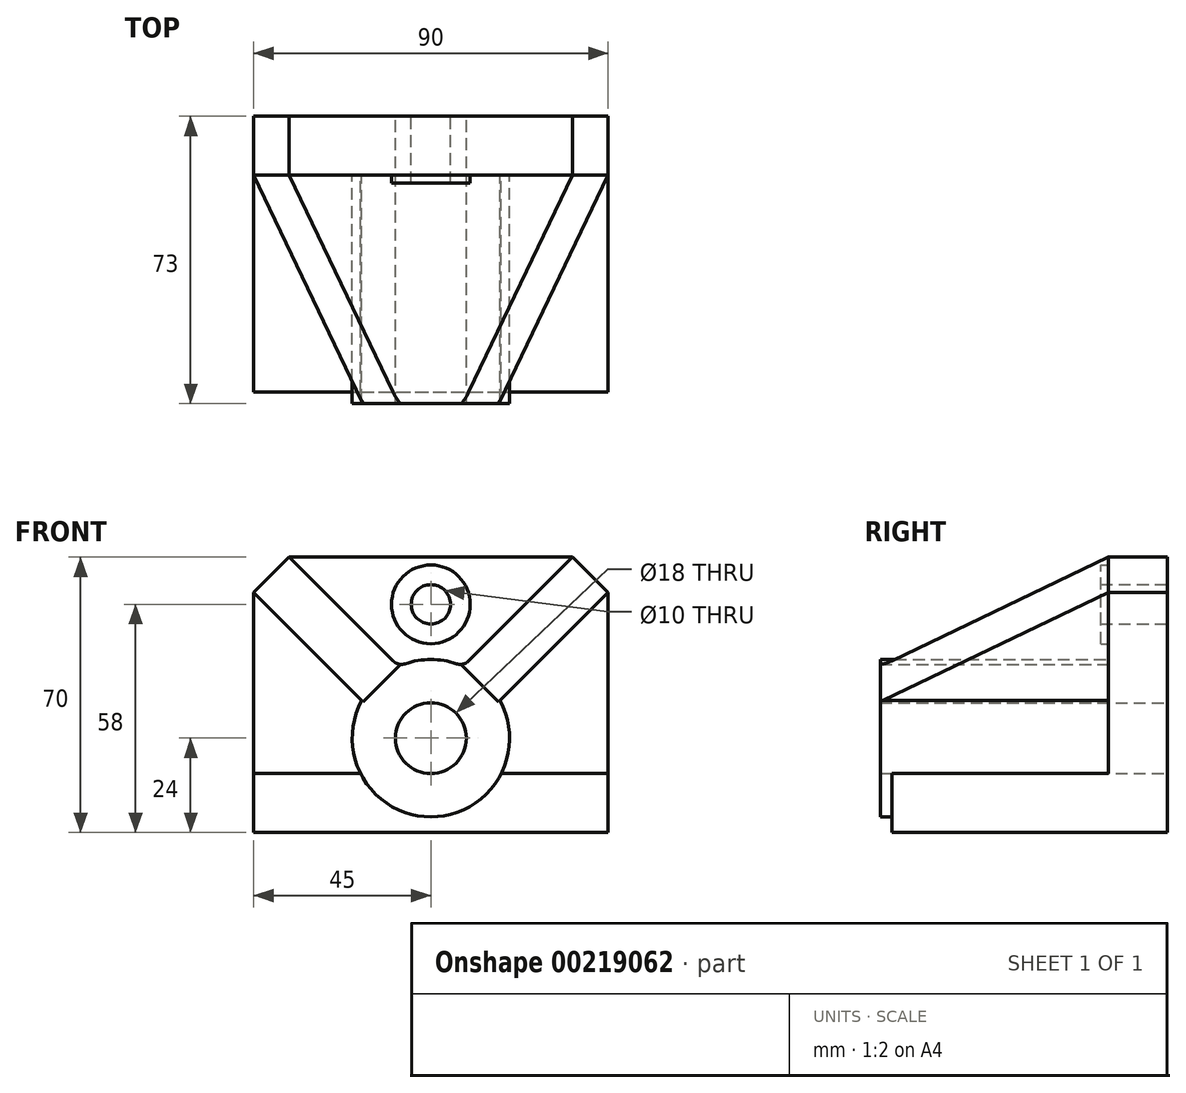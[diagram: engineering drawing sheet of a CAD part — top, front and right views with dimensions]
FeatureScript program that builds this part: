
annotation { "Feature Type Name" : "Feature", "Feature Type Description" : "" }
export const myFeature = defineFeature(function(context is Context, id is Id, definition is map)
    precondition{}
    {
        {
            var Q0;
            Q0=qCreatedBy(makeId("Front.planeOp"),FACE);
            var sketch = newSketch(context, id + "F0", { "sketchPlane" : qUnion([Q0])});
            skLineSegment(sketch, "E0", {"start": v(0, 0) * mm, "end": v(90, 0) * mm});
            skLineSegment(sketch, "E1", {"start": v(90, 0) * mm, "end": v(90, 70) * mm});
            skLineSegment(sketch, "E2", {"start": v(0, 70) * mm, "end": v(0, 0) * mm});
            skCircle(sketch, "E3", {"center": v(45, 24) * mm, "radius": 20 * mm});
            skCircle(sketch, "E4", {"center": v(45, 24) * mm, "radius": 9 * mm});
            skCircle(sketch, "E5", {"center": v(45, 58) * mm, "radius": 5 * mm});
            skCircle(sketch, "E6", {"center": v(45, 58) * mm, "radius": 10 * mm});
            skLineSegment(sketch, "E7", {"start": v(0, 15) * mm, "end": v(27.14, 15) * mm});
            skLineSegment(sketch, "E8", {"start": v(0, 70) * mm, "end": v(90, 70) * mm});
            skLineSegment(sketch, "E9.trimOffspring", {"start": v(62.86, 15) * mm, "end": v(90, 15) * mm});
            skSolve(sketch);
        }
        {
            var Q0;
            Q0=makeQuery(id+"F0.imprint","IMPRINT",FACE,{"disambiguationData":[TD([[makeQuery(id+"F0.imprint","IMPRINT",EDGE,{"derivedFrom":sQuery(id+"F0.wireOp",EDGE,"E6")}),-1.0]])]});
            extrude(context, id + "F1", {"entities" : qUnion([Q0]), "depth" : 15 * mm});
        }
        {
            var Q0;
            {var subQ4=sQuery(id+"F0.wireOp",EDGE,"E0");Q0=makeQuery(id+"F0.imprint","IMPRINT",FACE,{"disambiguationData":[TD([[makeQuery(id+"F0.imprint","IMPRINT",EDGE,{"derivedFrom":subQ4}),1.0]])]});}
            extrude(context, id + "F2", {"entities" : qUnion([Q0]), "operationType" : NewBodyOperationType.ADD, "depth" : 70 * mm});
        }
        {
            var Q0;
            Q0=makeQuery(id+"F0.imprint","IMPRINT",FACE,{"disambiguationData":[TD([[makeQuery(id+"F0.imprint","IMPRINT",EDGE,{"derivedFrom":sQuery(id+"F0.wireOp",EDGE,"E4")}),-1.0]])]});
            extrude(context, id + "F3", {"entities" : qUnion([Q0]), "operationType" : NewBodyOperationType.ADD, "depth" : 73 * mm});
        }
        {
            var Q0;
            Q0=makeQuery(id+"F0.imprint","IMPRINT",FACE,{"disambiguationData":[TD([[makeQuery(id+"F0.imprint","IMPRINT",EDGE,{"derivedFrom":sQuery(id+"F0.wireOp",EDGE,"E5")}),-1.0]])]});
            extrude(context, id + "F4", {"entities" : qUnion([Q0]), "operationType" : NewBodyOperationType.ADD, "depth" : 17 * mm});
        }
        {
            var Q0;
            Q0=makeQuery(id+"F1.opExtrude","SWEPT_EDGE",EDGE,{"disambiguationData":[OSD([sQuery(id+"F0.wireOp",EDGE,"E1"),sQuery(id+"F0.wireOp",EDGE,"E8")])]});
            var Q1;
            Q1=makeQuery(id+"F1.opExtrude","SWEPT_EDGE",EDGE,{"disambiguationData":[OSD([sQuery(id+"F0.wireOp",EDGE,"E2"),sQuery(id+"F0.wireOp",EDGE,"E8")])]});
            chamfer(context, id + "F5", {"entities" : qUnion([Q0, Q1]), "chamferType" : ChamferType.TWO_OFFSETS, "width1" : 9 * mm, "oppositeDirection" : false, "width2" : 9 * mm, "tangentPropagation" : true});
        }
        {
            var Q0;
            Q0=makeQuery(id+"F1.opExtrude","CAP_FACE",FACE,{"disambiguationData":[OSD([sQuery(id+"F0.wireOp",EDGE,"E1"),sQuery(id+"F0.wireOp",EDGE,"E2"),sQuery(id+"F0.wireOp",EDGE,"E3"),sQuery(id+"F0.wireOp",EDGE,"E6"),sQuery(id+"F0.wireOp",EDGE,"E7"),sQuery(id+"F0.wireOp",EDGE,"E8"),sQuery(id+"F0.wireOp",EDGE,"E9.trimOffspring")])],"isStart":false});
            var sketch = newSketch(context, id + "F6", { "sketchPlane" : qUnion([Q0])});
            skLineSegment(sketch, "E10", {"start": v(81, 70) * mm, "end": v(53.23, 42.23) * mm});
            skLineSegment(sketch, "E11", {"start": v(90, 61) * mm, "end": v(62.56, 33.56) * mm});
            skLineSegment(sketch, "E12.0", {"start": v(90, 61) * mm, "end": v(81, 70) * mm});
            skArc(sketch, "E13.0", {"start": v(62.56, 33.56) * mm, "mid": v(58.6, 38.66) * mm, "end": v(53.23, 42.23) * mm});
            skLineSegment(sketch, "E14", {"start": v(45, 24) * mm, "end": v(45, 94.83) * mm});
            skLineSegment(sketch, "E15.MirrorCS", {"start": v(9, 70) * mm, "end": v(36.77, 42.23) * mm});
            skLineSegment(sketch, "E16.MirrorCS", {"start": v(0, 61) * mm, "end": v(27.44, 33.56) * mm});
            skLineSegment(sketch, "E17.MirrorCS", {"start": v(0, 61) * mm, "end": v(9, 70) * mm});
            skArc(sketch, "E18.MirrorCS", {"start": v(27.44, 33.56) * mm, "mid": v(31.4, 38.66) * mm, "end": v(36.77, 42.23) * mm});
            skSolve(sketch);
        }
        {
            var Q0;
            Q0 = qSketchRegion(id + "F6", true);
            var Q1;
            Q1=makeQuery(id+"F3.opExtrude","CAP_FACE",FACE,{"disambiguationData":[OSD([sQuery(id+"F0.wireOp",EDGE,"E3"),sQuery(id+"F0.wireOp",EDGE,"E4")])],"isStart":false});
            extrude(context, id + "F7", {"entities" : qUnion([Q0]), "operationType" : NewBodyOperationType.ADD, "endBound" : BoundingType.UP_TO_SURFACE, "endBoundEntityFace" : qUnion([Q1]), "depth" : 25 * mm});
        }
        {
            var Q0;
            Q0=makeQuery(id+"F7.opExtrude","SWEPT_FACE",FACE,{"disambiguationData":[OSD([sQuery(id+"F6.wireOp",EDGE,"E10")])]});
            var sketch = newSketch(context, id + "F8", { "sketchPlane" : qUnion([Q0])});
            skLineSegment(sketch, "E19.0", {"start": v(73, 106.77) * mm, "end": v(15, 106.77) * mm});
            skLineSegment(sketch, "E20.0", {"start": v(73, 106.77) * mm, "end": v(73, 67.5) * mm});
            skLineSegment(sketch, "E21", {"start": v(15, 106.77) * mm, "end": v(73, 67.5) * mm});
            skSolve(sketch);
        }
        {
            var Q0;
            Q0=makeQuery(id+"F8.imprint","IMPRINT",FACE,{"disambiguationData":[TD([[makeQuery(id+"F8.imprint","IMPRINT",EDGE,{"derivedFrom":sQuery(id+"F8.wireOp",EDGE,"E19.0")}),1.0]])]});
            var Q1;
            Q1=makeQuery(id+"F7.opExtrude","SWEPT_FACE",FACE,{"disambiguationData":[OSD([sQuery(id+"F6.wireOp",EDGE,"E11")])]});
            extrude(context, id + "F9", {"entities" : qUnion([Q0]), "operationType" : NewBodyOperationType.REMOVE, "endBound" : BoundingType.UP_TO_SURFACE, "oppositeDirection" : true, "endBoundEntityFace" : qUnion([Q1]), "depth" : 25 * mm});
        }
        {
            var Q0;
            Q0=makeQuery(id+"F7.opExtrude","SWEPT_FACE",FACE,{"disambiguationData":[OSD([sQuery(id+"F6.wireOp",EDGE,"E15.MirrorCS")])]});
            var sketch = newSketch(context, id + "F10", { "sketchPlane" : qUnion([Q0])});
            skLineSegment(sketch, "E22", {"start": v(-15, 43.13) * mm, "end": v(-73, 3.86) * mm});
            skLineSegment(sketch, "E23", {"start": v(-73, 3.86) * mm, "end": v(-73, 43.13) * mm});
            skLineSegment(sketch, "E24", {"start": v(-73, 43.13) * mm, "end": v(-15, 43.13) * mm});
            skSolve(sketch);
        }
        {
            var Q0;
            Q0 = qSketchRegion(id + "F10", true);
            var Q1;
            Q1=makeQuery(id+"F7.opExtrude","SWEPT_FACE",FACE,{"disambiguationData":[OSD([sQuery(id+"F6.wireOp",EDGE,"E16.MirrorCS")])]});
            extrude(context, id + "F11", {"entities" : qUnion([Q0]), "operationType" : NewBodyOperationType.REMOVE, "endBound" : BoundingType.UP_TO_SURFACE, "oppositeDirection" : true, "endBoundEntityFace" : qUnion([Q1]), "depth" : 25 * mm});
        }
        {
            var Q0;
            Q0=makeQuery(id+"F7.opExtrude","SWEPT_EDGE",EDGE,{"disambiguationData":[OSD([sQuery(id+"F0.wireOp",EDGE,"E3"),sQuery(id+"F6.wireOp",EDGE,"E15.MirrorCS"),sQuery(id+"F6.wireOp",EDGE,"E18.MirrorCS")])]});
            var Q1;
            Q1=makeQuery(id+"F7.opExtrude","SWEPT_EDGE",EDGE,{"disambiguationData":[OSD([sQuery(id+"F0.wireOp",EDGE,"E3"),sQuery(id+"F6.wireOp",EDGE,"E10"),sQuery(id+"F6.wireOp",EDGE,"E13.0")])]});
            var Q2;
            Q2=makeQuery(id+"F2.opExtrude","SWEPT_EDGE",EDGE,{"disambiguationData":[OSD([sQuery(id+"F0.wireOp",EDGE,"E3"),sQuery(id+"F0.wireOp",EDGE,"E9.trimOffspring")])]});
            var Q3;
            Q3=makeQuery(id+"F2.opExtrude","SWEPT_EDGE",EDGE,{"disambiguationData":[OSD([sQuery(id+"F0.wireOp",EDGE,"E3"),sQuery(id+"F0.wireOp",EDGE,"E7")])]});
            var Q4;
            {var subQ0=sQuery(id+"F0.wireOp",EDGE,"E3");Q4=makeQuery(id+"F7.boolean.opBoolean","SPLIT",EDGE,{"disambiguationData":[TD([makeQuery(id+"F7.opExtrude","SWEPT_FACE",FACE,{"disambiguationData":[OSD([sQuery(id+"F6.wireOp",EDGE,"E10")])]})])],"derivedFrom":makeQuery(id+"F1.opExtrude","CAP_EDGE",EDGE,{"disambiguationData":[OSD([subQ0])],"isStart":false})});}
            var Q5;
            {var subQ0=sQuery(id+"F0.wireOp",EDGE,"E9.trimOffspring");var subQ1=sQuery(id+"F0.wireOp",EDGE,"E3");Q5=makeQuery(id+"F7.boolean.opBoolean","SPLIT",EDGE,{"disambiguationData":[TD([makeQuery(id+"F2.opExtrude","SWEPT_FACE",FACE,{"disambiguationData":[OSD([subQ0])]})])],"derivedFrom":makeQuery(id+"F1.opExtrude","CAP_EDGE",EDGE,{"disambiguationData":[OSD([subQ1])],"isStart":false})});}
            var Q6;
            {var subQ0=sQuery(id+"F0.wireOp",EDGE,"E7");var subQ1=sQuery(id+"F0.wireOp",EDGE,"E3");Q6=makeQuery(id+"F7.boolean.opBoolean","SPLIT",EDGE,{"disambiguationData":[TD([makeQuery(id+"F2.opExtrude","SWEPT_FACE",FACE,{"disambiguationData":[OSD([subQ0])]})])],"derivedFrom":makeQuery(id+"F1.opExtrude","CAP_EDGE",EDGE,{"disambiguationData":[OSD([subQ1])],"isStart":false})});}
            var Q7;
            {var subQ0=sQuery(id+"F6.wireOp",EDGE,"E16.MirrorCS");var subQ1=sQuery(id+"F0.wireOp",EDGE,"E3");Q7=makeQuery(id+"F11.boolean.opBoolean","SPLIT",EDGE,{"disambiguationData":[TD([makeQuery(id+"F1.opExtrude","CAP_FACE",FACE,{"disambiguationData":[OSD([sQuery(id+"F0.wireOp",EDGE,"E1"),sQuery(id+"F0.wireOp",EDGE,"E2"),subQ1,sQuery(id+"F0.wireOp",EDGE,"E6"),sQuery(id+"F0.wireOp",EDGE,"E7"),sQuery(id+"F0.wireOp",EDGE,"E8"),sQuery(id+"F0.wireOp",EDGE,"E9.trimOffspring")])],"isStart":false})])],"derivedFrom":makeQuery(id+"F7.opExtrude","SWEPT_EDGE",EDGE,{"disambiguationData":[OSD([subQ1,subQ0,sQuery(id+"F6.wireOp",EDGE,"E18.MirrorCS")])]})});}
            var Q8;
            {var subQ0=sQuery(id+"F6.wireOp",EDGE,"E11");var subQ1=sQuery(id+"F0.wireOp",EDGE,"E3");Q8=makeQuery(id+"F9.boolean.opBoolean","SPLIT",EDGE,{"disambiguationData":[TD([makeQuery(id+"F1.opExtrude","CAP_FACE",FACE,{"disambiguationData":[OSD([sQuery(id+"F0.wireOp",EDGE,"E1"),sQuery(id+"F0.wireOp",EDGE,"E2"),subQ1,sQuery(id+"F0.wireOp",EDGE,"E6"),sQuery(id+"F0.wireOp",EDGE,"E7"),sQuery(id+"F0.wireOp",EDGE,"E8"),sQuery(id+"F0.wireOp",EDGE,"E9.trimOffspring")])],"isStart":false})])],"derivedFrom":makeQuery(id+"F7.opExtrude","SWEPT_EDGE",EDGE,{"disambiguationData":[OSD([subQ1,subQ0,sQuery(id+"F6.wireOp",EDGE,"E13.0")])]})});}
            fillet(context, id + "F12", {"entities" : qUnion([Q0, Q1, Q2, Q3, Q4, Q5, Q6, Q7, Q8]), "radius" : 3 * mm, "tangentPropagation" : true, "allowEdgeOverflow" : false});
        }
    });
